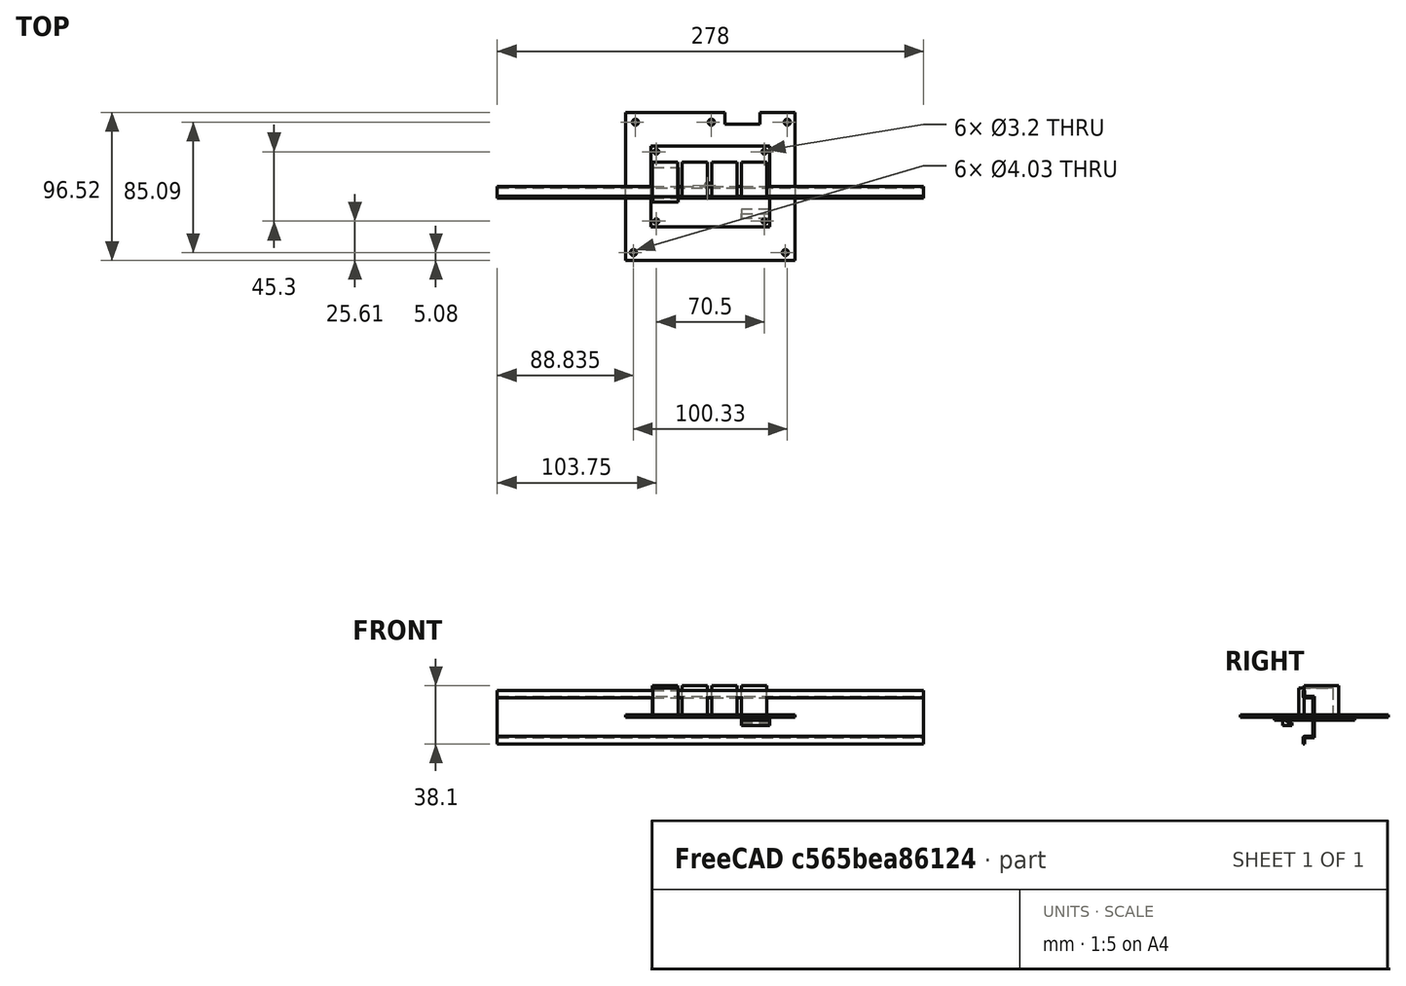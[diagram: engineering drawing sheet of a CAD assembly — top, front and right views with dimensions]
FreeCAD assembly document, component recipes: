
FREECAD ASSEMBLY — COMPONENT RECIPES ("autopool_box_vertical19")

This assembly document has 4 components, labeled P0..P3 below (a component is one placed body or linked part). 4 of them carry a construction recipe — the FreeCAD feature program that regenerates the part from scratch, quoted from this document or its linked companion documents; the rest are supplied as boundary geometry only. No exploded tour is included for this assembly.
COMPONENT P0 — recipe-attached ("support001", modeled in this document).
Construction recipe (the document's own serialized feature program — sketch geometry with constraints, then the solid features built on it; lengths are millimeters unless a unit is written):

FEATURE [PartDesign::ShapeBinder] ShapeBinder
  Support = -> [LinearPattern]
  TraceSupport = false
FEATURE [Sketcher::SketchObject] Sketch006
  ExternalGeometry = -> [ShapeBinder]
  MapMode = 5
  Placement = pos=(0,0,0) rot=(1,0,0;3.14159rad)
  Support = -> [ShapeBinder]
  sketch-geometry (6):
    g0: LineSegment StartX=38.75 StartY=26.25 StartZ=0 EndX=20.2255 EndY=26.25 EndZ=0
    g1: LineSegment StartX=20.2255 StartY=26.25 StartZ=0 EndX=20.2255 EndY=-26.25 EndZ=0
    g2: LineSegment StartX=20.2255 StartY=-26.25 StartZ=0 EndX=38.75 EndY=-26.25 EndZ=0
    g3: LineSegment StartX=38.75 StartY=-26.25 StartZ=0 EndX=38.75 EndY=26.25 EndZ=0
    g4: Circle CenterX=35.25 CenterY=-22.65 CenterZ=0 NormalX=0 NormalY=0 NormalZ=1 AngleXU=0 Radius=1.6
    g5: Circle CenterX=35.25 CenterY=22.65 CenterZ=0 NormalX=0 NormalY=0 NormalZ=1 AngleXU=0 Radius=1.6
  constraints (12):
    c: Coincident(g0,g1)
    c: Coincident(g1,g2)
    c: Coincident(g2,g3)
    c: Coincident(g3,g0)
    c: Horizontal(g0)
    c: Horizontal(g2)
    c: Vertical(g1)
    c: Vertical(g3)
    c: Coincident(g0,g-4)
    c: PointOnObject(g1,g-5)
    c: Coincident(g4,g-6)
    c: Coincident(g5,g-7)
FEATURE [PartDesign::Pad] Pad006
  AllowMultiFace = false
  Length = 2
  Length2 = 100
  Profile = -> Sketch006
  Type = 0
FEATURE [PartDesign::Body] Body005  label="base"
  Group = -> [ShapeBinder,Sketch006,Pad006]
  Origin = -> Origin009
  Tip = -> Pad006
FEATURE [PartDesign::ShapeBinder] ShapeBinder001
  Placement = pos=(0,0,-2) rot=(0,0,1;0rad)
  Support = -> [Pad006]
  TraceSupport = false
FEATURE [Sketcher::SketchObject] Sketch009
  ExternalGeometry = -> [ShapeBinder001]
  MapMode = 5
  Placement = pos=(0,0,-2) rot=(1,0,0;3.14159rad)
  Support = -> [ShapeBinder001]
  sketch-geometry (4):
    g0: LineSegment StartX=20.2255 StartY=-17.8362 StartZ=0 EndX=38.75 EndY=-17.8362 EndZ=0
    g1: LineSegment StartX=38.75 StartY=-17.8362 StartZ=0 EndX=38.75 EndY=-20.8846 EndZ=0
    g2: LineSegment StartX=38.75 StartY=-20.8846 StartZ=0 EndX=20.2255 EndY=-20.8846 EndZ=0
    g3: LineSegment StartX=20.2255 StartY=-20.8846 StartZ=0 EndX=20.2255 EndY=-17.8362 EndZ=0
  constraints (10):
    c: Coincident(g0,g1)
    c: Coincident(g1,g2)
    c: Coincident(g2,g3)
    c: Coincident(g3,g0)
    c: Horizontal(g0)
    c: Horizontal(g2)
    c: Vertical(g1)
    c: Vertical(g3)
    c: PointOnObject(g0,g-3)
    c: PointOnObject(g1,g-4)
FEATURE [PartDesign::Pad] Pad009
  AllowMultiFace = false
  Length = 1.5
  Length2 = 100
  Placement = pos=(0,0,-2) rot=(0,0,1;0rad)
  Profile = -> Sketch009
  Type = 0
FEATURE [Sketcher::SketchObject] Sketch010
  ExternalGeometry = -> [Pad009]
  MapMode = 5
  Placement = pos=(0,0,-3.5) rot=(1,0,0;3.14159rad)
  Support = -> [Pad009]
  sketch-geometry (4):
    g0: LineSegment StartX=20.2255 StartY=-20.8846 StartZ=0 EndX=38.75 EndY=-20.8846 EndZ=0
    g1: LineSegment StartX=38.75 StartY=-20.8846 StartZ=0 EndX=38.75 EndY=-14.8508 EndZ=0
    g2: LineSegment StartX=38.75 StartY=-14.8508 StartZ=0 EndX=20.2255 EndY=-14.8508 EndZ=0
    g3: LineSegment StartX=20.2255 StartY=-14.8508 StartZ=0 EndX=20.2255 EndY=-20.8846 EndZ=0
  constraints (10):
    c: Coincident(g0,g1)
    c: Coincident(g1,g2)
    c: Coincident(g2,g3)
    c: Coincident(g3,g0)
    c: Horizontal(g0)
    c: Horizontal(g2)
    c: Vertical(g1)
    c: Vertical(g3)
    c: Coincident(g0,g-3)
    c: PointOnObject(g1,g-4)
FEATURE [PartDesign::Pad] Pad010
  AllowMultiFace = false
  BaseFeature = -> Pad009
  Length = 2
  Length2 = 100
  Placement = pos=(0,0,-2) rot=(0,0,1;0rad)
  Profile = -> Sketch010
  Type = 0
FEATURE [PartDesign::Body] Body006
  Group = -> [ShapeBinder001,Sketch009,Pad009,Sketch010,Pad010]
  Origin = -> Origin010
  Tip = -> Pad010
COMPONENT P1 — recipe-attached ("relays4_part", modeled in this document).
Construction recipe (the document's own serialized feature program — sketch geometry with constraints, then the solid features built on it; lengths are millimeters unless a unit is written):

FEATURE [Sketcher::SketchObject] Sketch
  MapMode = 5
  Support = -> [XY_Plane001]
  sketch-geometry (12):
    g0: LineSegment StartX=-38.75 StartY=26.25 StartZ=0 EndX=38.75 EndY=26.25 EndZ=0
    g1: LineSegment StartX=38.75 StartY=26.25 StartZ=0 EndX=38.75 EndY=-26.25 EndZ=0
    g2: LineSegment StartX=38.75 StartY=-26.25 StartZ=0 EndX=-38.75 EndY=-26.25 EndZ=0
    g3: LineSegment StartX=-38.75 StartY=-26.25 StartZ=0 EndX=-38.75 EndY=26.25 EndZ=0
    g4: Circle CenterX=-35.25 CenterY=22.65 CenterZ=0 NormalX=0 NormalY=0 NormalZ=1 AngleXU=0 Radius=1.6
    g5: Circle CenterX=-35.25 CenterY=-22.65 CenterZ=0 NormalX=0 NormalY=0 NormalZ=1 AngleXU=0 Radius=1.6
    g6: Circle CenterX=35.25 CenterY=22.65 CenterZ=0 NormalX=0 NormalY=0 NormalZ=1 AngleXU=0 Radius=1.6
    g7: Circle CenterX=35.25 CenterY=-22.65 CenterZ=0 NormalX=0 NormalY=0 NormalZ=1 AngleXU=0 Radius=1.6
    g8: LineSegment [constr] StartX=-35.25 StartY=22.65 StartZ=0 EndX=35.25 EndY=22.65 EndZ=0
    g9: LineSegment [constr] StartX=35.25 StartY=22.65 StartZ=0 EndX=35.25 EndY=-22.65 EndZ=0
    g10: LineSegment [constr] StartX=35.25 StartY=-22.65 StartZ=0 EndX=-35.25 EndY=-22.65 EndZ=0
    g11: LineSegment [constr] StartX=-35.25 StartY=-22.65 StartZ=0 EndX=-35.25 EndY=22.65 EndZ=0
  constraints (31):
    c: Coincident(g0,g1)
    c: Coincident(g1,g2)
    c: Coincident(g2,g3)
    c: Coincident(g3,g0)
    c: Horizontal(g0)
    c: Horizontal(g2)
    c: Vertical(g1)
    c: Vertical(g3)
    c: Symmetric(g0,g1,g-1)
    c: DistanceX(g0,g0) = 77.5
    c: DistanceY(g1,g0) = 52.5
    c: DistanceY(g4,g0) = 3.6
    c: DistanceX(g0,g4) = 3.5
    c: Diameter(g4) = 3.2
    c: Equal(g4,g5)
    c: Equal(g5,g7)
    c: Equal(g7,g6)
    c: Coincident(g8,g9)
    c: Coincident(g9,g10)
    c: Coincident(g10,g11)
    c: Coincident(g11,g8)
    c: Horizontal(g8)
    c: Horizontal(g10)
    c: Vertical(g9)
    c: Vertical(g11)
    c: Coincident(g8,g4)
    c: DistanceX(g9,g1) = 3.5
    c: DistanceY(g1,g9) = 3.6
    c: Coincident(g6,g8)
    c: Coincident(g5,g10)
    c: Coincident(g7,g9)
FEATURE [PartDesign::Pad] Pad
  AllowMultiFace = false
  Length = 1.6
  Length2 = 100
  Profile = -> Sketch
  Type = 0
FEATURE [Sketcher::SketchObject] Sketch003
  MapMode = 5
  Support = -> [XY_Plane006]
  sketch-geometry (4):
    g0: LineSegment StartX=-37.6149 StartY=12.2539 StartZ=0 EndX=-21.1149 EndY=12.2539 EndZ=0
    g1: LineSegment StartX=-21.1149 StartY=12.2539 StartZ=0 EndX=-21.1149 EndY=-10.2461 EndZ=0
    g2: LineSegment StartX=-21.1149 StartY=-10.2461 StartZ=0 EndX=-37.6149 EndY=-10.2461 EndZ=0
    g3: LineSegment StartX=-37.6149 StartY=-10.2461 StartZ=0 EndX=-37.6149 EndY=12.2539 EndZ=0
  constraints (10):
    c: Coincident(g0,g1)
    c: Coincident(g1,g2)
    c: Coincident(g2,g3)
    c: Coincident(g3,g0)
    c: Horizontal(g0)
    c: Horizontal(g2)
    c: Vertical(g1)
    c: Vertical(g3)
    c: DistanceY(g1,g1) = 22.5
    c: DistanceX(g2,g2) = 16.5
FEATURE [PartDesign::Pad] Pad003
  AllowMultiFace = false
  Length = 19
  Length2 = 100
  Profile = -> Sketch003
  Type = 0
FEATURE [PartDesign::Body] Body003
  Group = -> [Sketch003,Pad003]
  Origin = -> Origin006
  Tip = -> Pad003
FEATURE [Sketcher::SketchObject] Sketch004
  MapMode = 5
  Placement = pos=(0,0,1.6) rot=(0,0,1;0rad)
  Support = -> [Pad]
  sketch-geometry (4):
    g0: LineSegment StartX=-37.75 StartY=15.7124 StartZ=0 EndX=-21.25 EndY=15.7124 EndZ=0
    g1: LineSegment StartX=-21.25 StartY=15.7124 StartZ=0 EndX=-21.25 EndY=-6.78761 EndZ=0
    g2: LineSegment StartX=-21.25 StartY=-6.78761 StartZ=0 EndX=-37.75 EndY=-6.78761 EndZ=0
    g3: LineSegment StartX=-37.75 StartY=-6.78761 StartZ=0 EndX=-37.75 EndY=15.7124 EndZ=0
  constraints (10):
    c: Coincident(g0,g1)
    c: Coincident(g1,g2)
    c: Coincident(g2,g3)
    c: Coincident(g3,g0)
    c: Horizontal(g0)
    c: Horizontal(g2)
    c: Vertical(g1)
    c: Vertical(g3)
    c: DistanceY(g1,g1) = 22.5
    c: DistanceX(g0,g0) = 16.5
FEATURE [PartDesign::Pad] Pad004
  AllowMultiFace = false
  BaseFeature = -> Pad
  Length = 19
  Length2 = 100
  Profile = -> Sketch004
  Type = 0
FEATURE [PartDesign::LinearPattern] LinearPattern
  BaseFeature = -> Pad004
  Direction = -> X_Axis001
  Length = 58
  Occurrences = 4
  Originals = -> [Pad004]
FEATURE [PartDesign::Body] Body
  Group = -> [Sketch,Pad,Sketch004,Pad004,LinearPattern]
  Origin = -> Origin001
  Tip = -> LinearPattern
COMPONENT P2 — recipe-attached ("autopool_part", modeled in this document).
Construction recipe (the document's own serialized feature program — sketch geometry with constraints, then the solid features built on it; lengths are millimeters unless a unit is written):

FEATURE [Sketcher::SketchObject] Sketch001
  MapMode = 5
  Support = -> [XY_Plane003]
  sketch-geometry (16):
    g0: LineSegment StartX=-55.245 StartY=48.26 StartZ=0 EndX=9.525 EndY=48.26 EndZ=0
    g1: LineSegment StartX=9.525 StartY=48.26 StartZ=0 EndX=9.525 EndY=40.64 EndZ=0
    g2: LineSegment StartX=9.525 StartY=40.64 StartZ=0 EndX=32.385 EndY=40.64 EndZ=0
    g3: LineSegment StartX=32.385 StartY=40.64 StartZ=0 EndX=32.385 EndY=48.26 EndZ=0
    g4: LineSegment StartX=32.385 StartY=48.26 StartZ=0 EndX=55.245 EndY=48.26 EndZ=0
    g5: LineSegment StartX=55.245 StartY=48.26 StartZ=0 EndX=55.245 EndY=-48.26 EndZ=0
    g6: LineSegment StartX=55.245 StartY=-48.26 StartZ=0 EndX=-55.245 EndY=-48.26 EndZ=0
    g7: LineSegment StartX=-55.245 StartY=-48.26 StartZ=0 EndX=-55.245 EndY=48.26 EndZ=0
    g8: LineSegment [constr] StartX=-48.895 StartY=41.91 StartZ=0 EndX=50.165 EndY=41.91 EndZ=0
    g9: LineSegment [constr] StartX=-50.165 StartY=-43.18 StartZ=0 EndX=48.895 EndY=-43.18 EndZ=0
    g10: Circle CenterX=-48.895 CenterY=41.91 CenterZ=0 NormalX=0 NormalY=0 NormalZ=1 AngleXU=0 Radius=2.015
    g11: Circle CenterX=-50.165 CenterY=-43.18 CenterZ=0 NormalX=0 NormalY=0 NormalZ=1 AngleXU=0 Radius=2.015
    g12: Circle CenterX=48.895 CenterY=-43.18 CenterZ=0 NormalX=0 NormalY=0 NormalZ=1 AngleXU=0 Radius=2.015
    g13: Circle CenterX=50.165 CenterY=41.91 CenterZ=0 NormalX=0 NormalY=0 NormalZ=1 AngleXU=0 Radius=2.015
    g14: Circle CenterX=0.635 CenterY=41.91 CenterZ=0 NormalX=0 NormalY=0 NormalZ=1 AngleXU=0 Radius=2.015
    g15: Circle CenterX=-1.905 CenterY=0.635 CenterZ=0 NormalX=0 NormalY=0 NormalZ=1 AngleXU=0 Radius=2.015
  constraints (45):
    c: Horizontal(g0)
    c: Coincident(g0,g1)
    c: Vertical(g1)
    c: Coincident(g1,g2)
    c: Horizontal(g2)
    c: Coincident(g2,g3)
    c: Vertical(g3)
    c: Coincident(g3,g4)
    c: Horizontal(g4)
    c: Coincident(g4,g5)
    c: Vertical(g5)
    c: Coincident(g5,g6)
    c: Horizontal(g6)
    c: Coincident(g6,g7)
    c: Coincident(g7,g0)
    c: Vertical(g7)
    c: Equal(g5,g7)
    c: DistanceY(g5,g4) = 96.52
    c: DistanceX(g3,g4) = 22.86
    c: DistanceX(g1,g2) = 22.86
    c: DistanceY(g1,g0) = 7.62
    c: DistanceX(g0,g0) = 64.77
    c: Symmetric(g0,g5,g-1)
    c: Horizontal(g8)
    c: DistanceY(g8,g0) = 6.35
    c: DistanceX(g8,g4) = 5.08
    c: DistanceX(g0,g8) = 6.35
    c: Horizontal(g9)
    c: DistanceX(g9,g5) = 6.35
    c: DistanceX(g6,g9) = 5.08
    c: DistanceY(g5,g9) = 5.08
    c: Coincident(g10,g8)
    c: Coincident(g11,g9)
    c: Coincident(g12,g9)
    c: Coincident(g13,g8)
    c: PointOnObject(g14,g8)
    c: Equal(g10,g14)
    c: Equal(g14,g13)
    c: Equal(g13,g12)
    c: Equal(g12,g11)
    c: Equal(g15,g13)
    c: Diameter(g15) = 4.03
    c: DistanceX(g14,g1) = 8.89
    c: DistanceX(g15,g5) = 57.15
    c: DistanceY(g5,g15) = 48.895
FEATURE [PartDesign::Pad] Pad001
  AllowMultiFace = false
  Length = 1.6
  Length2 = 100
  Profile = -> Sketch001
  Type = 0
FEATURE [PartDesign::Body] Body001
  Group = -> [Sketch001,Pad001]
  Origin = -> Origin003
  Tip = -> Pad001
COMPONENT P3 — recipe-attached ("din_rail_part", modeled in this document).
Construction recipe (the document's own serialized feature program — sketch geometry with constraints, then the solid features built on it; lengths are millimeters unless a unit is written):

FEATURE [Sketcher::SketchObject] Sketch005
  MapMode = 5
  Placement = pos=(0,0,0) rot=(0.57735,0.57735,0.57735;2.0944rad)
  Support = -> [YZ_Plane007]
  sketch-geometry (12):
    g0: LineSegment StartX=0 StartY=13.5 StartZ=0 EndX=0 EndY=-13.5 EndZ=0
    g1: LineSegment StartX=0 StartY=-13.5 StartZ=0 EndX=-6.5 EndY=-13.5 EndZ=0
    g2: LineSegment StartX=-6.5 StartY=-13.5 StartZ=0 EndX=-6.5 EndY=-17.5 EndZ=0
    g3: LineSegment StartX=-6.5 StartY=-17.5 StartZ=0 EndX=-7.5 EndY=-17.5 EndZ=0
    g4: LineSegment StartX=-7.5 StartY=-17.5 StartZ=0 EndX=-7.5 EndY=-12.5 EndZ=0
    g5: LineSegment StartX=-7.5 StartY=-12.5 StartZ=0 EndX=-1 EndY=-12.5 EndZ=0
    g6: LineSegment StartX=-1 StartY=-12.5 StartZ=0 EndX=-1 EndY=12.5 EndZ=0
    g7: LineSegment StartX=-1 StartY=12.5 StartZ=0 EndX=-7.5 EndY=12.5 EndZ=0
    g8: LineSegment StartX=-7.5 StartY=12.5 StartZ=0 EndX=-7.5 EndY=17.5 EndZ=0
    g9: LineSegment StartX=-7.5 StartY=17.5 StartZ=0 EndX=-6.5 EndY=17.5 EndZ=0
    g10: LineSegment StartX=-6.5 StartY=17.5 StartZ=0 EndX=-6.5 EndY=13.5 EndZ=0
    g11: LineSegment StartX=-6.5 StartY=13.5 StartZ=0 EndX=0 EndY=13.5 EndZ=0
  constraints (34):
    c: PointOnObject(g0,g-2)
    c: PointOnObject(g0,g-2)
    c: Coincident(g0,g1)
    c: Horizontal(g1)
    c: Coincident(g1,g2)
    c: Vertical(g2)
    c: Coincident(g2,g3)
    c: Coincident(g3,g4)
    c: Vertical(g4)
    c: Coincident(g4,g5)
    c: Horizontal(g5)
    c: Coincident(g5,g6)
    c: Coincident(g6,g7)
    c: Horizontal(g7)
    c: Coincident(g7,g8)
    c: Vertical(g8)
    c: Coincident(g8,g9)
    c: Coincident(g9,g10)
    c: Coincident(g10,g11)
    c: Coincident(g11,g0)
    c: Horizontal(g11)
    c: Horizontal(g9)
    c: Horizontal(g3)
    c: Equal(g9,g3)
    c: DistanceX(g6,g0) = 1
    c: DistanceX(g8,g9) = 1
    c: DistanceY(g7,g10) = 1
    c: DistanceY(g1,g4) = 1
    c: Symmetric(g6,g5,g-1)
    c: Equal(g11,g1)
    c: DistanceY(g3,g8) = 35
    c: DistanceX(g3,g0) = 7.5
    c: DistanceY(g0,g0) = 27
    c: Symmetric(g9,g2,g-1)
FEATURE [PartDesign::Pad] Pad005
  AllowMultiFace = false
  Length = 278
  Length2 = 100
  Midplane = true
  Placement = pos=(0,0,0) rot=(0.57735,0.57735,0.57735;2.0944rad)
  Profile = -> Sketch005
  Type = 0
FEATURE [PartDesign::Fillet] Fillet
  Base = -> Pad005 [Edge14]
  BaseFeature = -> Pad005
  Placement = pos=(0,0,0) rot=(0.57735,0.57735,0.57735;2.0944rad)
  Radius = 1
  SupportTransform = false
FEATURE [PartDesign::Fillet] Fillet001
  Base = -> Fillet [Edge35]
  BaseFeature = -> Fillet
  Placement = pos=(0,0,0) rot=(0.57735,0.57735,0.57735;2.0944rad)
  Radius = 1
  SupportTransform = false
FEATURE [PartDesign::Body] Body004
  Group = -> [Sketch005,Pad005,Fillet,Fillet001]
  Origin = -> Origin007
  Tip = -> Fillet001
PROVENANCE & LICENSES
A FreeCAD (.FCStd) document from a public repository crawl; recipes are the document's own serialized feature recipes (and, for linked parts, companion documents' recipes).
License: as declared in the source repository (recorded in the dataset sidecar).
